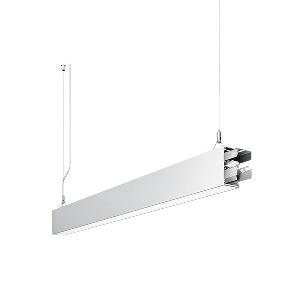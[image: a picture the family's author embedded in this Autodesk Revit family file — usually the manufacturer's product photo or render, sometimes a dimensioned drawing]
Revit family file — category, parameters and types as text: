
# Revit family: dotoo_line_-_dlp_2000_830_d_sta_00805806_cbed
name_source: partatom
category: Lighting Fixtures
units: mm (PartAtom-declared; Revit-internal decimal feet)

## family parameters
Cut with Voids When Loaded = No
Host = Face
Light Source = No
Part Type = Normal
Room Calculation Point = No
Round Connector Dimension = Use Diameter
Shared = No

## types (1)
- DOTOO.line - DLP 2000/830/D STA (1 x LED, 1650 lm, 3000K)
    Apparent Load = 16 VA
    Approval mark = CE
    CIE Flux Codes = 67 91 98 100 100
    Color Rendering = 80-89
    Color Temperature = 3000K
    Control Gear = Electronic ballast
    Default Elevation = 1800 mm
    Description = DLP 2000/830/D|Suspended luminaire|light source: LED|connected load: 220-240 V, 50/60 Hz|Power consumption: approx. 16 W|standby: approx. 0,15|luminous flux: 1650 lm|luminous efficacy: 103 lm/W|light distribution: Direct|direct ratio: approx. 100 %|colour temperature: Warm white, ca. 3000 K|color rendering index (CRI): >= 80|chromaticity tolerance:  3 SDCM|System of protection: IP 40|technology: Continuously dimmable|luminaire body|material: Sectional aluminium|colour: White|lamp cover: Acrylic (PMMA), Clear|mains lead: 2.00 m With free stranded wires|Fastening: Steel cable 0.3 - 0.7 m|glare control: Prism aperture|luminance(L65): <= 3000 cd/m|unified glare rating(4H 8H): <=  19|special features: DALI Load 1x, TouchDIM - dimming via standard switch, Through-wired, up to 18 m on one mains connection, Flicker-free, Suitable as emergency lighting, Start luminaire with mains connection, Mechanical and electrical connection of the individual modules without tools|
    Frequency = 50 Hz
    Height = 110 mm
    Lamp = 1 x LED
    Lamp Light Flux = 1650 lm
    Lamp count = 1
    Length = 1408 mm
    Luminous efficacy = 103 lm/W
    Manufacturer = Waldmann
    ModVariant = No
    Model = 00805806
    Mounting Place = Ceiling
    Mounting Type = Pendant
    Number of Poles = 1
    OnlyDefault = Yes
    Power Factor = 1
    Product Name = DOTOO.line - DLP 2000/830/D STA
    Product group = Suspended luminaire
    ProductGroupID = 9
    Protection Class = Protection class I
    Protection Degree = IP 40
    RLX_Detail_Level = 1
    RLX_Emergency_Light_Flux = 0 lm
    RLX_Emergency_Type = 0
    RLX_Emergency_Type_DB = No
    RlxData = <blob elided: 22141 chars, md5=ca74d818>
    Socket = socket
    Standby Power = 0 W
    System Light Flux = 1650 lm
    System Power = 16 W
    Type Comments = Product without accessories
    Type Image = 113307000-00692585.jpg
    URL = http://relux.com
    VarID = ---
    Voltage = 230 V
    Voltage Range = 220-240 V
    Weight = 0.00 kg
    Width = 60 mm  [stored 0.19685 ft]

note: [stored X ft] marks values corroborated as IEEE doubles in the binary element streams (Revit-internal decimal feet)

## geometry (parser evidence)
native form markers: Blend x4, Sweep x12
no freeform markers — native parametric forms only
